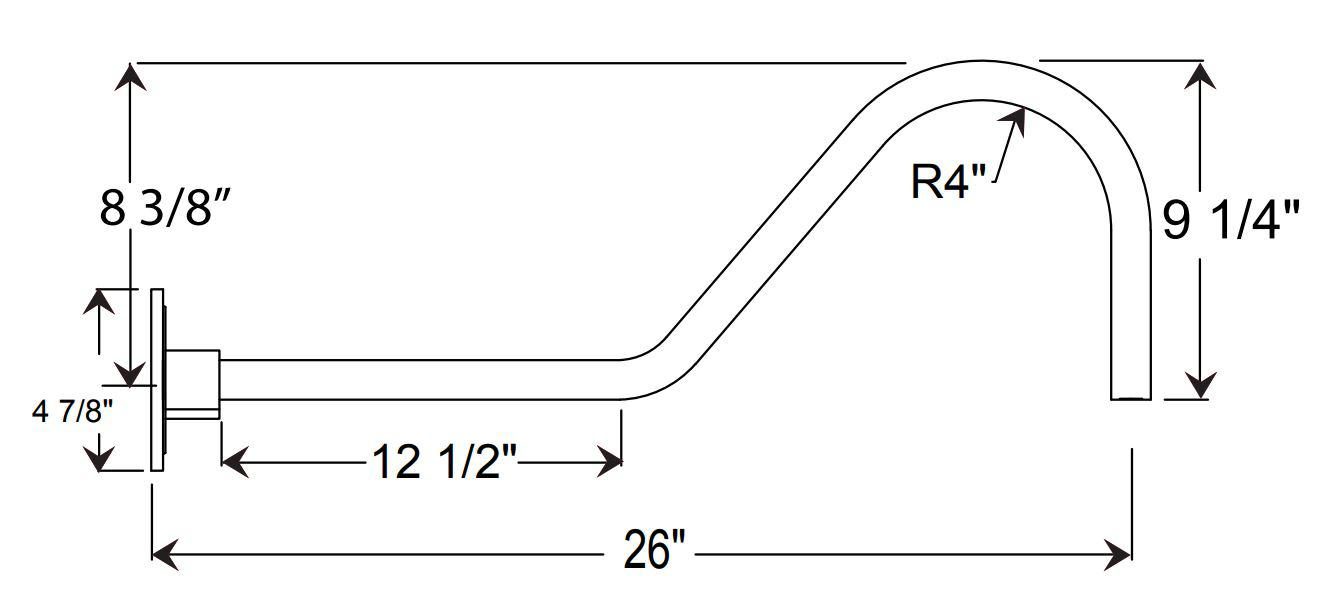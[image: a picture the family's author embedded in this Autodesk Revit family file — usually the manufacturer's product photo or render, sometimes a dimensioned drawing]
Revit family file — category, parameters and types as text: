
# Revit family: Orbitor 200w -16,18,20 LED
name_source: partatom
category: Lighting Fixtures
units: mm (PartAtom-declared; Revit-internal decimal feet)

## family parameters
Always vertical = Yes
Cut with Voids When Loaded = No
Light Source = Yes
OmniClass Number = 23.80.70.00
OmniClass Title = Lighting
Part Type = Normal
Room Calculation Point = No
Round Connector Dimension = Use Diameter
Shared = No
Work Plane-Based = No

## types (3) — shared parameters
Apparent Load = 24 VA
Body Colour = Spun aluminium
Body Material = body
Bulb = Bulb
CRI = >90
Color Filter = 16777215
Construction Material = Heavy Duty spun aluminum.
Default Elevation = 0' - 0"
Description = 120-277 Voltage
Dimming = 1%
Dimming Lamp Color Temperature Shift = <None>
Efficiency = 65-125 lumens per watt
Fixture Height = 1' - 2"
INSIDE BODY = INSIDE BODY
Lamp = LED
Life = L70 50,000 hours
Load Classification = Lighting
Manufacturer = ANP Lighting
Power Factor = 1
Tilt Angle = 90.00°
URL = https://www.anplighting.com
Voltage = 277 V
Warranty = 5 year limited warranty
Wattage Comments = 24W
Weight = 4.0 lbs

## per-type parameters (varying)
| type | Fixture Diameter | ORB216 | ORB218 | ORB220 | Photometric Web File |
| ORB216 | 1' - 4" | Yes | No | No | ORB216CLM016LDDW40K.IES |
| ORB218 | 1' - 6" | No | Yes | No | ORB216CLM016LDDW40K.IES |
| ORB220 | 1' - 8" | No | No | Yes | ORB220CLM024LDDW40K.IES |

note: column(s) folded — value = type name in every type: Model

## geometry (parser evidence)
native form markers: Sweep x26
no freeform markers — native parametric forms only
